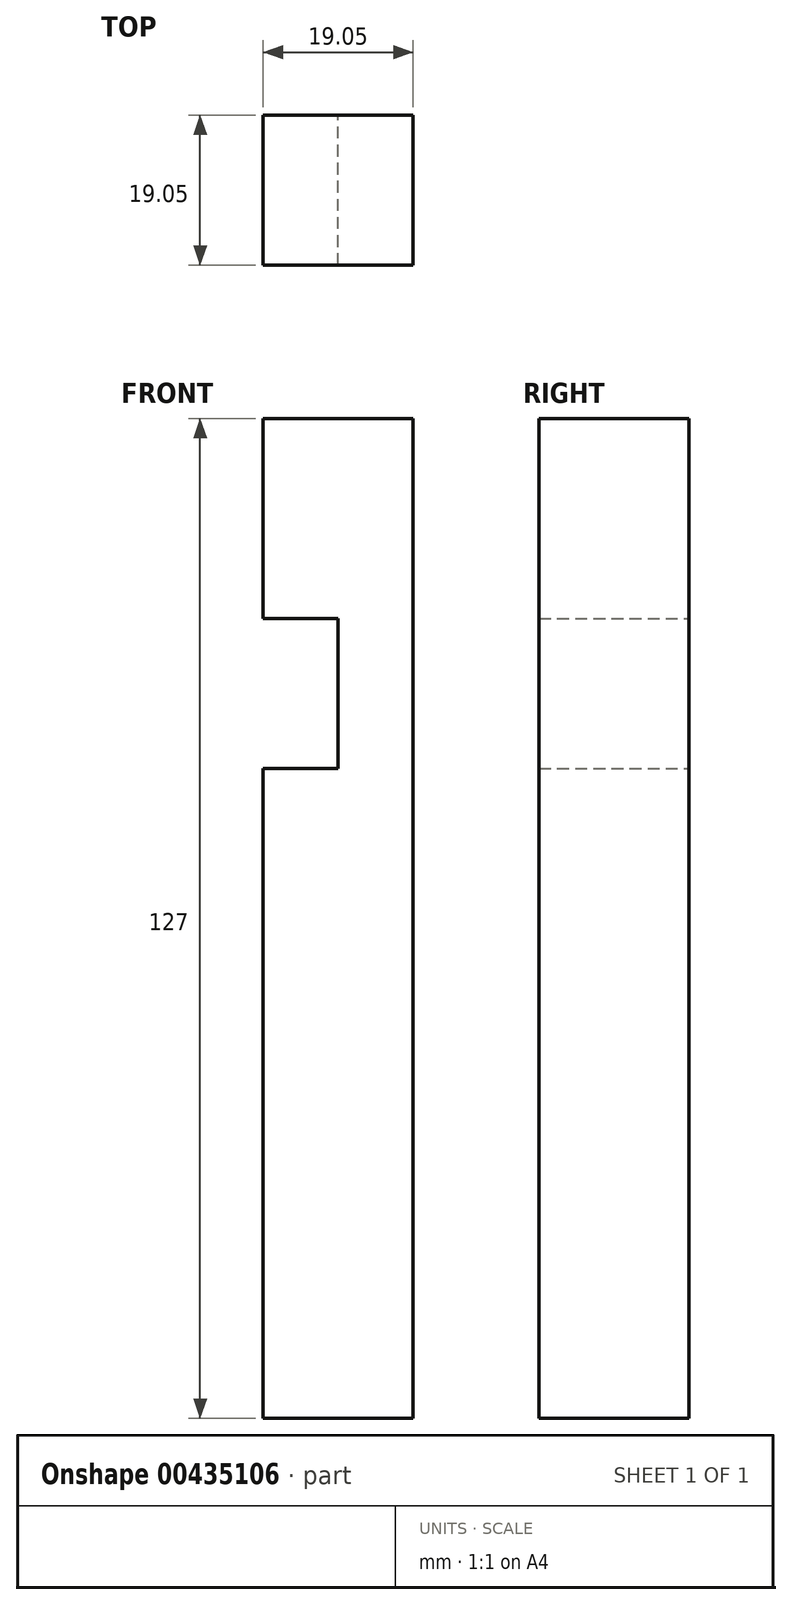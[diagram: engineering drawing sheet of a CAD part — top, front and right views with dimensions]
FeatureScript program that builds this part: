
annotation { "Feature Type Name" : "Feature", "Feature Type Description" : "" }
export const myFeature = defineFeature(function(context is Context, id is Id, definition is map)
    precondition{}
    {
        {
            var Q0;
            Q0=qCreatedBy(makeId("Front.planeOp"),FACE);
            var sketch = newSketch(context, id + "F0", { "sketchPlane" : qUnion([Q0])});
            skLineSegment(sketch, "E0", {"start": v(29.01, -52.98) * mm, "end": v(29.01, 74.02) * mm});
            skLineSegment(sketch, "E1", {"start": v(29.01, -52.98) * mm, "end": v(9.96, -52.98) * mm});
            skLineSegment(sketch, "E2", {"start": v(29.01, 74.02) * mm, "end": v(9.96, 74.02) * mm});
            skLineSegment(sketch, "E3", {"start": v(9.96, 74.02) * mm, "end": v(9.96, 48.62) * mm});
            skLineSegment(sketch, "E4", {"start": v(9.96, 48.62) * mm, "end": v(19.49, 48.62) * mm});
            skLineSegment(sketch, "E5", {"start": v(19.49, 48.62) * mm, "end": v(19.49, 29.57) * mm});
            skLineSegment(sketch, "E6", {"start": v(19.49, 29.57) * mm, "end": v(9.96, 29.57) * mm});
            skLineSegment(sketch, "E7", {"start": v(9.96, 29.57) * mm, "end": v(9.96, -52.98) * mm});
            skSolve(sketch);
        }
        {
            var Q0;
            Q0=qSketchRegion(id+"F0",true);
            extrude(context, id + "F1", {"entities" : qUnion([Q0]), "depth" : 19.05 * mm});
        }
    });
